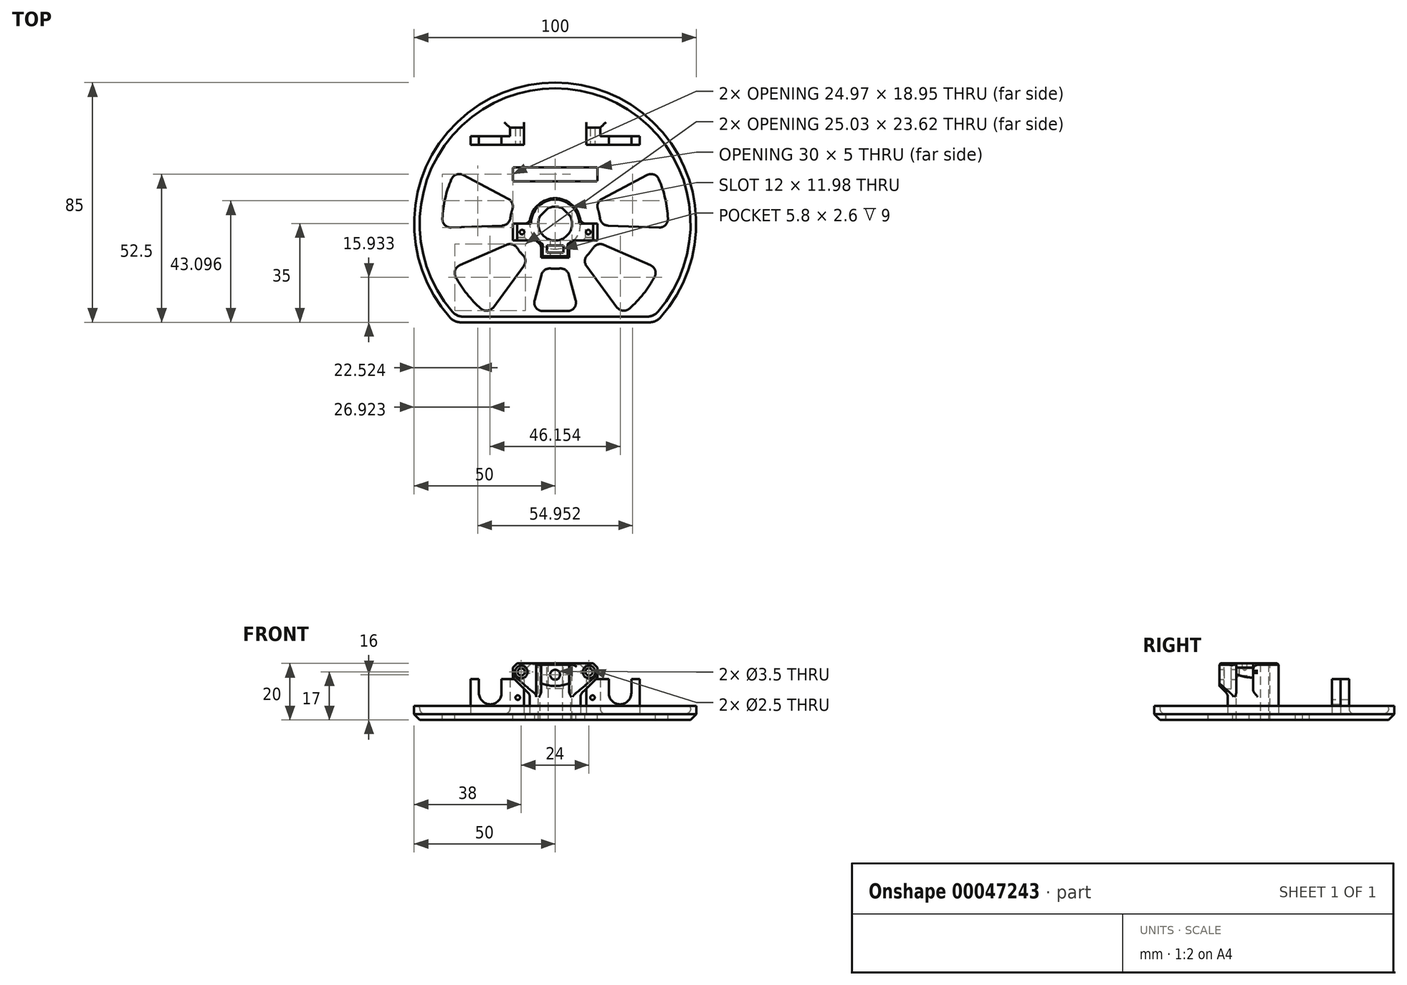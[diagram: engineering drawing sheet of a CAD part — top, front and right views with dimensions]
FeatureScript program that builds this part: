
annotation { "Feature Type Name" : "Feature", "Feature Type Description" : "" }
export const myFeature = defineFeature(function(context is Context, id is Id, definition is map)
    precondition{}
    {
        {
            var Q0;
            Q0=qCreatedBy(makeId("Top.planeOp"),FACE);
            var sketch = newSketch(context, id + "F0", { "sketchPlane" : qUnion([Q0])});
            skArc(sketch, "E0", {"start": v(35.7, -35) * mm, "mid": v(0, 50) * mm, "end": v(-35.7, -35) * mm});
            skLineSegment(sketch, "E1", {"start": v(0, 0) * mm, "end": v(0, -35) * mm, "construction": true});
            skLineSegment(sketch, "E2", {"start": v(0, -35) * mm, "end": v(35.7, -35) * mm});
            skLineSegment(sketch, "E3", {"start": v(0, -35) * mm, "end": v(-35.7, -35) * mm});
            skSolve(sketch);
        }
        {
            var Q0;
            Q0 = qSketchRegion(id + "F0", true);
            extrude(context, id + "F1", {"entities" : qUnion([Q0]), "depth" : 5 * mm});
        }
        {
            var Q0;
            Q0=makeQuery(id+"F1.opExtrude","CAP_FACE",FACE,{"disambiguationData":[OSD([sQuery(id+"F0.wireOp",EDGE,"E0")])],"isStart":false});
            var sketch = newSketch(context, id + "F2", { "sketchPlane" : qUnion([Q0])});
            skArc(sketch, "E4", {"start": v(32.85, -35) * mm, "mid": v(0, 48) * mm, "end": v(-32.85, -35) * mm});
            skLineSegment(sketch, "E5.0", {"start": v(32.85, -35) * mm, "end": v(-32.85, -35) * mm, "construction": true});
            skLineSegment(sketch, "E6.0", {"start": v(32.85, -33) * mm, "end": v(-32.85, -33) * mm});
            skLineSegment(sketch, "E7", {"start": v(-32.85, -33) * mm, "end": v(-34.86, -33) * mm});
            skLineSegment(sketch, "E8", {"start": v(32.85, -33) * mm, "end": v(34.86, -33) * mm});
            skSolve(sketch);
        }
        {
            var Q0;
            Q0 = qSketchRegion(id + "F2", true);
            extrude(context, id + "F3", {"entities" : qUnion([Q0]), "operationType" : NewBodyOperationType.REMOVE, "oppositeDirection" : true, "depth" : 3 * mm});
        }
        {
            var Q0;
            Q0=makeQuery(id+"F3.boolean.opBoolean","COPY",EDGE,{"derivedFrom":makeQuery(id+"F3.opExtrude","SWEPT_EDGE",EDGE,{"disambiguationData":[OSD([sQuery(id+"F2.wireOp",EDGE,"E4"),sQuery(id+"F2.wireOp",EDGE,"E7")])]})});
            var Q1;
            Q1=makeQuery(id+"F3.boolean.opBoolean","COPY",EDGE,{"derivedFrom":makeQuery(id+"F3.opExtrude","SWEPT_EDGE",EDGE,{"disambiguationData":[OSD([sQuery(id+"F2.wireOp",EDGE,"E4"),sQuery(id+"F2.wireOp",EDGE,"E8")])]})});
            var Q2;
            Q2=makeQuery(id+"F1.opExtrude","SWEPT_EDGE",EDGE,{"disambiguationData":[OSD([sQuery(id+"F0.wireOp",EDGE,"E0"),sQuery(id+"F0.wireOp",EDGE,"E3")])]});
            var Q3;
            Q3=makeQuery(id+"F1.opExtrude","SWEPT_EDGE",EDGE,{"disambiguationData":[OSD([sQuery(id+"F0.wireOp",EDGE,"E0"),sQuery(id+"F0.wireOp",EDGE,"E2")])]});
            fillet(context, id + "F4", {"entities" : qUnion([Q0, Q1, Q2, Q3]), "radius" : 5 * mm, "tangentPropagation" : true, "allowEdgeOverflow" : false});
        }
        {
            var Q0;
            Q0=makeQuery(id+"F3.boolean.opBoolean","COPY",EDGE,{"derivedFrom":makeQuery(id+"F3.opExtrude","CAP_EDGE",EDGE,{"disambiguationData":[OSD([sQuery(id+"F2.wireOp",EDGE,"E4")])],"isStart":false})});
            var Q1;
            Q1=makeQuery(id+"F3.boolean.opBoolean","COPY",EDGE,{"derivedFrom":makeQuery(id+"F3.opExtrude","CAP_EDGE",EDGE,{"disambiguationData":[OSD([sQuery(id+"F2.wireOp",EDGE,"E6.0"),sQuery(id+"F2.wireOp",EDGE,"E7"),sQuery(id+"F2.wireOp",EDGE,"E8")])],"isStart":false})});
            fillet(context, id + "F5", {"entities" : qUnion([Q0, Q1]), "radius" : 2 * mm, "tangentPropagation" : true, "allowEdgeOverflow" : false});
        }
        {
            var Q0;
            Q0=makeQuery(id+"F1.opExtrude","CAP_EDGE",EDGE,{"disambiguationData":[OSD([sQuery(id+"F0.wireOp",EDGE,"E0")])],"isStart":true});
            chamfer(context, id + "F6", {"entities" : qUnion([Q0]), "width" : 2 * mm, "tangentPropagation" : true});
        }
        {
            var Q0;
            Q0=makeQuery(id+"F3.boolean.opBoolean","COPY",FACE,{"derivedFrom":makeQuery(id+"F3.opExtrude","CAP_FACE",FACE,{"disambiguationData":[OSD([sQuery(id+"F2.wireOp",EDGE,"E4")])],"isStart":false})});
            var sketch = newSketch(context, id + "F7", { "sketchPlane" : qUnion([Q0])});
            skCircle(sketch, "E9", {"center": v(0, 0) * mm, "radius": 6 * mm});
            skCircle(sketch, "E10.0", {"center": v(0, 0) * mm, "radius": 50 * mm, "construction": true});
            skLineSegment(sketch, "E11", {"start": v(0, 0) * mm, "end": v(0, -50) * mm, "construction": true});
            skArc(sketch, "E12.0", {"start": v(-10.35, -38.64) * mm, "mid": v(0, -40) * mm, "end": v(10.35, -38.64) * mm, "construction": true});
            skArc(sketch, "E13.0", {"start": v(-4.14, -15.45) * mm, "mid": v(0, -16) * mm, "end": v(4.14, -15.45) * mm});
            skLineSegment(sketch, "E14.trimOffspring", {"start": v(4.14, -15.45) * mm, "end": v(10.35, -38.64) * mm});
            skLineSegment(sketch, "E15.trimOffspring", {"start": v(-4.14, -15.45) * mm, "end": v(-10.35, -38.64) * mm});
            skLineSegment(sketch, "E16.1.0", {"start": v(9.5, -12.87) * mm, "end": v(23.75, -32.18) * mm});
            skLineSegment(sketch, "E16.1.1", {"start": v(14.66, -6.4) * mm, "end": v(36.66, -16) * mm});
            skArc(sketch, "E16.1.2", {"start": v(9.5, -12.87) * mm, "mid": v(12.5, -9.98) * mm, "end": v(14.66, -6.4) * mm});
            skArc(sketch, "E16.1.3", {"start": v(23.75, -32.18) * mm, "mid": v(31.27, -24.94) * mm, "end": v(36.66, -16) * mm});
            skLineSegment(sketch, "E16.2.0", {"start": v(15.99, -0.6) * mm, "end": v(39.97, -1.5) * mm});
            skLineSegment(sketch, "E16.2.1", {"start": v(14.15, 7.48) * mm, "end": v(35.36, 18.7) * mm});
            skArc(sketch, "E16.2.2", {"start": v(15.99, -0.6) * mm, "mid": v(15.6, 3.56) * mm, "end": v(14.15, 7.48) * mm});
            skArc(sketch, "E16.2.3", {"start": v(39.97, -1.5) * mm, "mid": v(39, 8.9) * mm, "end": v(35.36, 18.7) * mm});
            skLineSegment(sketch, "E16.5.0", {"start": v(-14.15, 7.48) * mm, "end": v(-35.36, 18.7) * mm});
            skLineSegment(sketch, "E16.5.1", {"start": v(-15.99, -0.6) * mm, "end": v(-39.97, -1.5) * mm});
            skArc(sketch, "E16.5.2", {"start": v(-14.15, 7.48) * mm, "mid": v(-15.6, 3.56) * mm, "end": v(-15.99, -0.6) * mm});
            skArc(sketch, "E16.5.3", {"start": v(-35.36, 18.7) * mm, "mid": v(-39, 8.9) * mm, "end": v(-39.97, -1.5) * mm});
            skLineSegment(sketch, "E16.6.0", {"start": v(-14.66, -6.4) * mm, "end": v(-36.66, -16) * mm});
            skLineSegment(sketch, "E16.6.1", {"start": v(-9.5, -12.87) * mm, "end": v(-23.75, -32.18) * mm});
            skArc(sketch, "E16.6.2", {"start": v(-14.66, -6.4) * mm, "mid": v(-12.5, -9.98) * mm, "end": v(-9.5, -12.87) * mm});
            skArc(sketch, "E16.6.3", {"start": v(-36.66, -16) * mm, "mid": v(-31.27, -24.94) * mm, "end": v(-23.75, -32.18) * mm});
            skLineSegment(sketch, "E17.trimOffspring", {"start": v(-8.3, -31) * mm, "end": v(8.3, -31) * mm});
            skSolve(sketch);
        }
        {
            var Q0;
            Q0 = qSketchRegion(id + "F7", true);
            extrude(context, id + "F8", {"entities" : qUnion([Q0]), "operationType" : NewBodyOperationType.REMOVE, "oppositeDirection" : true, "depth" : 25 * mm});
        }
        {
            var Q0;
            Q0=makeQuery(id+"F8.boolean.opBoolean","COPY",EDGE,{"derivedFrom":makeQuery(id+"F8.opExtrude","SWEPT_EDGE",EDGE,{"disambiguationData":[OSD([sQuery(id+"F7.wireOp",EDGE,"E16.6.1"),sQuery(id+"F7.wireOp",EDGE,"E16.6.2")])]})});
            var Q1;
            Q1=makeQuery(id+"F8.boolean.opBoolean","COPY",EDGE,{"derivedFrom":makeQuery(id+"F8.opExtrude","SWEPT_EDGE",EDGE,{"disambiguationData":[OSD([sQuery(id+"F7.wireOp",EDGE,"E16.6.0"),sQuery(id+"F7.wireOp",EDGE,"E16.6.2")])]})});
            var Q2;
            Q2=makeQuery(id+"F8.boolean.opBoolean","COPY",EDGE,{"derivedFrom":makeQuery(id+"F8.opExtrude","SWEPT_EDGE",EDGE,{"disambiguationData":[OSD([sQuery(id+"F7.wireOp",EDGE,"E16.6.0"),sQuery(id+"F7.wireOp",EDGE,"E16.6.3")])]})});
            var Q3;
            Q3=makeQuery(id+"F8.boolean.opBoolean","COPY",EDGE,{"derivedFrom":makeQuery(id+"F8.opExtrude","SWEPT_EDGE",EDGE,{"disambiguationData":[OSD([sQuery(id+"F7.wireOp",EDGE,"E16.6.1"),sQuery(id+"F7.wireOp",EDGE,"E16.6.3")])]})});
            var Q4;
            Q4=makeQuery(id+"F8.boolean.opBoolean","COPY",EDGE,{"derivedFrom":makeQuery(id+"F8.opExtrude","SWEPT_EDGE",EDGE,{"disambiguationData":[OSD([sQuery(id+"F7.wireOp",EDGE,"E12.0"),sQuery(id+"F7.wireOp",EDGE,"E15.trimOffspring")])]})});
            var Q5;
            Q5=makeQuery(id+"F8.boolean.opBoolean","COPY",EDGE,{"derivedFrom":makeQuery(id+"F8.opExtrude","SWEPT_EDGE",EDGE,{"disambiguationData":[OSD([sQuery(id+"F7.wireOp",EDGE,"E16.1.0"),sQuery(id+"F7.wireOp",EDGE,"E16.1.2")])]})});
            var Q6;
            Q6=makeQuery(id+"F8.boolean.opBoolean","COPY",EDGE,{"derivedFrom":makeQuery(id+"F8.opExtrude","SWEPT_EDGE",EDGE,{"disambiguationData":[OSD([sQuery(id+"F7.wireOp",EDGE,"E16.2.0"),sQuery(id+"F7.wireOp",EDGE,"E16.2.2")])]})});
            var Q7;
            Q7=makeQuery(id+"F8.boolean.opBoolean","COPY",EDGE,{"derivedFrom":makeQuery(id+"F8.opExtrude","SWEPT_EDGE",EDGE,{"disambiguationData":[OSD([sQuery(id+"F7.wireOp",EDGE,"E13.0"),sQuery(id+"F7.wireOp",EDGE,"E14.trimOffspring")])]})});
            var Q8;
            Q8=makeQuery(id+"F8.boolean.opBoolean","COPY",EDGE,{"derivedFrom":makeQuery(id+"F8.opExtrude","SWEPT_EDGE",EDGE,{"disambiguationData":[OSD([sQuery(id+"F7.wireOp",EDGE,"E16.2.1"),sQuery(id+"F7.wireOp",EDGE,"E16.2.3")])]})});
            var Q9;
            Q9=makeQuery(id+"F8.boolean.opBoolean","COPY",EDGE,{"derivedFrom":makeQuery(id+"F8.opExtrude","SWEPT_EDGE",EDGE,{"disambiguationData":[OSD([sQuery(id+"F7.wireOp",EDGE,"E16.1.1"),sQuery(id+"F7.wireOp",EDGE,"E16.1.3")])]})});
            var Q10;
            Q10=makeQuery(id+"F8.boolean.opBoolean","COPY",EDGE,{"derivedFrom":makeQuery(id+"F8.opExtrude","SWEPT_EDGE",EDGE,{"disambiguationData":[OSD([sQuery(id+"F7.wireOp",EDGE,"E12.0"),sQuery(id+"F7.wireOp",EDGE,"E14.trimOffspring")])]})});
            var Q11;
            Q11=makeQuery(id+"F8.boolean.opBoolean","COPY",EDGE,{"derivedFrom":makeQuery(id+"F8.opExtrude","SWEPT_EDGE",EDGE,{"disambiguationData":[OSD([sQuery(id+"F7.wireOp",EDGE,"E16.1.0"),sQuery(id+"F7.wireOp",EDGE,"E16.1.3")])]})});
            var Q12;
            Q12=makeQuery(id+"F8.boolean.opBoolean","COPY",EDGE,{"derivedFrom":makeQuery(id+"F8.opExtrude","SWEPT_EDGE",EDGE,{"disambiguationData":[OSD([sQuery(id+"F7.wireOp",EDGE,"E16.3.0"),sQuery(id+"F7.wireOp",EDGE,"E16.3.2")])]})});
            var Q13;
            Q13=makeQuery(id+"F8.boolean.opBoolean","COPY",EDGE,{"derivedFrom":makeQuery(id+"F8.opExtrude","SWEPT_EDGE",EDGE,{"disambiguationData":[OSD([sQuery(id+"F7.wireOp",EDGE,"E16.4.1"),sQuery(id+"F7.wireOp",EDGE,"E16.4.2")])]})});
            var Q14;
            Q14=makeQuery(id+"F8.boolean.opBoolean","COPY",EDGE,{"derivedFrom":makeQuery(id+"F8.opExtrude","SWEPT_EDGE",EDGE,{"disambiguationData":[OSD([sQuery(id+"F7.wireOp",EDGE,"E16.5.1"),sQuery(id+"F7.wireOp",EDGE,"E16.5.2")])]})});
            var Q15;
            Q15=makeQuery(id+"F8.boolean.opBoolean","COPY",EDGE,{"derivedFrom":makeQuery(id+"F8.opExtrude","SWEPT_EDGE",EDGE,{"disambiguationData":[OSD([sQuery(id+"F7.wireOp",EDGE,"E16.5.0"),sQuery(id+"F7.wireOp",EDGE,"E16.5.2")])]})});
            var Q16;
            Q16=makeQuery(id+"F8.boolean.opBoolean","COPY",EDGE,{"derivedFrom":makeQuery(id+"F8.opExtrude","SWEPT_EDGE",EDGE,{"disambiguationData":[OSD([sQuery(id+"F7.wireOp",EDGE,"E16.3.0"),sQuery(id+"F7.wireOp",EDGE,"E16.3.3")])]})});
            var Q17;
            Q17=makeQuery(id+"F8.boolean.opBoolean","COPY",EDGE,{"derivedFrom":makeQuery(id+"F8.opExtrude","SWEPT_EDGE",EDGE,{"disambiguationData":[OSD([sQuery(id+"F7.wireOp",EDGE,"E16.4.0"),sQuery(id+"F7.wireOp",EDGE,"E16.4.3")])]})});
            var Q18;
            Q18=makeQuery(id+"F8.boolean.opBoolean","COPY",EDGE,{"derivedFrom":makeQuery(id+"F8.opExtrude","SWEPT_EDGE",EDGE,{"disambiguationData":[OSD([sQuery(id+"F7.wireOp",EDGE,"E16.4.0"),sQuery(id+"F7.wireOp",EDGE,"E16.4.2")])]})});
            var Q19;
            Q19=makeQuery(id+"F8.boolean.opBoolean","COPY",EDGE,{"derivedFrom":makeQuery(id+"F8.opExtrude","SWEPT_EDGE",EDGE,{"disambiguationData":[OSD([sQuery(id+"F7.wireOp",EDGE,"E16.3.1"),sQuery(id+"F7.wireOp",EDGE,"E16.3.2")])]})});
            var Q20;
            Q20=makeQuery(id+"F8.boolean.opBoolean","COPY",EDGE,{"derivedFrom":makeQuery(id+"F8.opExtrude","SWEPT_EDGE",EDGE,{"disambiguationData":[OSD([sQuery(id+"F7.wireOp",EDGE,"E16.5.1"),sQuery(id+"F7.wireOp",EDGE,"E16.5.3")])]})});
            var Q21;
            Q21=makeQuery(id+"F8.boolean.opBoolean","COPY",EDGE,{"derivedFrom":makeQuery(id+"F8.opExtrude","SWEPT_EDGE",EDGE,{"disambiguationData":[OSD([sQuery(id+"F7.wireOp",EDGE,"E16.5.0"),sQuery(id+"F7.wireOp",EDGE,"E16.5.3")])]})});
            var Q22;
            Q22=makeQuery(id+"F8.boolean.opBoolean","COPY",EDGE,{"derivedFrom":makeQuery(id+"F8.opExtrude","SWEPT_EDGE",EDGE,{"disambiguationData":[OSD([sQuery(id+"F7.wireOp",EDGE,"E13.0"),sQuery(id+"F7.wireOp",EDGE,"E15.trimOffspring")])]})});
            var Q23;
            Q23=makeQuery(id+"F8.boolean.opBoolean","COPY",EDGE,{"derivedFrom":makeQuery(id+"F8.opExtrude","SWEPT_EDGE",EDGE,{"disambiguationData":[OSD([sQuery(id+"F7.wireOp",EDGE,"E16.3.1"),sQuery(id+"F7.wireOp",EDGE,"E16.3.3")])]})});
            var Q24;
            Q24=makeQuery(id+"F8.boolean.opBoolean","COPY",EDGE,{"derivedFrom":makeQuery(id+"F8.opExtrude","SWEPT_EDGE",EDGE,{"disambiguationData":[OSD([sQuery(id+"F7.wireOp",EDGE,"E16.2.1"),sQuery(id+"F7.wireOp",EDGE,"E16.2.2")])]})});
            var Q25;
            Q25=makeQuery(id+"F8.boolean.opBoolean","COPY",EDGE,{"derivedFrom":makeQuery(id+"F8.opExtrude","SWEPT_EDGE",EDGE,{"disambiguationData":[OSD([sQuery(id+"F7.wireOp",EDGE,"E16.1.1"),sQuery(id+"F7.wireOp",EDGE,"E16.1.2")])]})});
            var Q26;
            Q26=makeQuery(id+"F8.boolean.opBoolean","COPY",EDGE,{"derivedFrom":makeQuery(id+"F8.opExtrude","SWEPT_EDGE",EDGE,{"disambiguationData":[OSD([sQuery(id+"F7.wireOp",EDGE,"E16.2.0"),sQuery(id+"F7.wireOp",EDGE,"E16.2.3")])]})});
            var Q27;
            Q27=makeQuery(id+"F8.boolean.opBoolean","COPY",EDGE,{"derivedFrom":makeQuery(id+"F8.opExtrude","SWEPT_EDGE",EDGE,{"disambiguationData":[OSD([sQuery(id+"F7.wireOp",EDGE,"E16.4.1"),sQuery(id+"F7.wireOp",EDGE,"E16.4.3")])]})});
            var Q28;
            Q28=makeQuery(id+"F8.boolean.opBoolean","COPY",EDGE,{"derivedFrom":makeQuery(id+"F8.opExtrude","SWEPT_EDGE",EDGE,{"disambiguationData":[OSD([sQuery(id+"F2.wireOp",EDGE,"E4"),sQuery(id+"F2.wireOp",EDGE,"E6.0"),sQuery(id+"F2.wireOp",EDGE,"E7"),sQuery(id+"F2.wireOp",EDGE,"E8"),sQuery(id+"F7.wireOp",EDGE,"E15.trimOffspring"),sQuery(id+"F7.wireOp",EDGE,"E17.trimOffspring")])]})});
            var Q29;
            Q29=makeQuery(id+"F8.boolean.opBoolean","COPY",EDGE,{"derivedFrom":makeQuery(id+"F8.opExtrude","SWEPT_EDGE",EDGE,{"disambiguationData":[OSD([sQuery(id+"F2.wireOp",EDGE,"E4"),sQuery(id+"F2.wireOp",EDGE,"E6.0"),sQuery(id+"F2.wireOp",EDGE,"E7"),sQuery(id+"F2.wireOp",EDGE,"E8"),sQuery(id+"F7.wireOp",EDGE,"E14.trimOffspring"),sQuery(id+"F7.wireOp",EDGE,"E17.trimOffspring")])]})});
            fillet(context, id + "F9", {"entities" : qUnion([Q0, Q1, Q2, Q3, Q4, Q5, Q6, Q7, Q8, Q9, Q10, Q11, Q12, Q13, Q14, Q15, Q16, Q17, Q18, Q19, Q20, Q21, Q22, Q23, Q24, Q25, Q26, Q27, Q28, Q29]), "radius" : 3 * mm, "tangentPropagation" : true, "allowEdgeOverflow" : false});
        }
        {
            var Q0;
            Q0=qCreatedBy(makeId("Top.planeOp"),FACE);
            var sketch = newSketch(context, id + "F10", { "sketchPlane" : qUnion([Q0])});
            skLineSegment(sketch, "E18", {"start": v(2.59, 5.41) * mm, "end": v(5.41, 2.59) * mm});
            skLineSegment(sketch, "E19", {"start": v(-2.59, 5.41) * mm, "end": v(-5.41, 2.59) * mm});
            skLineSegment(sketch, "E20", {"start": v(0, -8) * mm, "end": v(0, 0) * mm});
            skCircle(sketch, "E21", {"center": v(0, 0) * mm, "radius": 9 * mm});
            skArc(sketch, "E22.0", {"start": v(2.59, 5.41) * mm, "mid": v(0, 6) * mm, "end": v(-2.59, 5.41) * mm});
            skArc(sketch, "E23.trimOffspring", {"start": v(-5.41, 2.59) * mm, "mid": v(0, -6) * mm, "end": v(5.41, 2.59) * mm});
            skLineSegment(sketch, "E24", {"start": v(0, 0) * mm, "end": v(-5, 0) * mm, "construction": true});
            skLineSegment(sketch, "E25", {"start": v(-5, 0) * mm, "end": v(-5, -12) * mm});
            skLineSegment(sketch, "E26", {"start": v(-5, -12) * mm, "end": v(5, -12) * mm});
            skLineSegment(sketch, "E27", {"start": v(5, -12) * mm, "end": v(5, 0) * mm});
            skLineSegment(sketch, "E28", {"start": v(5, 0) * mm, "end": v(0, 0) * mm, "construction": true});
            skLineSegment(sketch, "E29", {"start": v(-9, 0) * mm, "end": v(-15, 0) * mm});
            skLineSegment(sketch, "E30", {"start": v(-15, 0) * mm, "end": v(-15, -6) * mm});
            skLineSegment(sketch, "E31", {"start": v(-15, -6) * mm, "end": v(-6.7, -6) * mm});
            skLineSegment(sketch, "E32.MirrorCS", {"start": v(9, 0) * mm, "end": v(15, 0) * mm});
            skLineSegment(sketch, "E33.MirrorCS", {"start": v(15, -6) * mm, "end": v(6.7, -6) * mm});
            skLineSegment(sketch, "E34.MirrorCS", {"start": v(15, 0) * mm, "end": v(15, -6) * mm});
            skSolve(sketch);
        }
        {
            var Q0;
            {var subQ11=sQuery(id+"F10.wireOp",EDGE,"E18");Q0=makeQuery(id+"F10.imprint","IMPRINT",FACE,{"disambiguationData":[TD([[makeQuery(id+"F10.imprint","IMPRINT",EDGE,{"derivedFrom":subQ11}),1.0]])]});}
            var Q1;
            {var subQ3=sQuery(id+"F10.wireOp",EDGE,"E23.trimOffspring");var subQ5=makeQuery(id+"F10.imprint","IMPRINT",VERTEX,{"derivedFrom":subQ3});Q1=makeQuery(id+"F10.imprint","IMPRINT",FACE,{"disambiguationData":[TD([[makeQuery(id+"F10.imprint","IMPRINT",EDGE,{"disambiguationData":[TD([[subQ5,1.0]])],"derivedFrom":subQ3}),-1.0]])]});}
            var Q2;
            {var subQ5=sQuery(id+"F10.wireOp",EDGE,"E26");Q2=makeQuery(id+"F10.imprint","IMPRINT",FACE,{"disambiguationData":[TD([[makeQuery(id+"F10.imprint","IMPRINT",EDGE,{"derivedFrom":subQ5}),1.0]])]});}
            extrude(context, id + "F11", {"entities" : qUnion([Q0, Q1, Q2]), "operationType" : NewBodyOperationType.ADD, "depth" : 20 * mm});
        }
        {
            var Q0;
            Q0=makeQuery(id+"F11.opExtrude","CAP_FACE",FACE,{"disambiguationData":[OSD([sQuery(id+"F10.wireOp",EDGE,"E18"),sQuery(id+"F10.wireOp",EDGE,"E19"),sQuery(id+"F10.wireOp",EDGE,"E21"),sQuery(id+"F10.wireOp",EDGE,"E22.0"),sQuery(id+"F10.wireOp",EDGE,"E23.trimOffspring"),sQuery(id+"F10.wireOp",EDGE,"E25"),sQuery(id+"F10.wireOp",EDGE,"E26"),sQuery(id+"F10.wireOp",EDGE,"E27")])],"isStart":false});
            var sketch = newSketch(context, id + "F12", { "sketchPlane" : qUnion([Q0])});
            skLineSegment(sketch, "E35", {"start": v(0, -9) * mm, "end": v(2.9, -9) * mm, "construction": true});
            skLineSegment(sketch, "E36", {"start": v(0, -9) * mm, "end": v(-2.9, -9) * mm, "construction": true});
            skLineSegment(sketch, "E37", {"start": v(-2.9, -9) * mm, "end": v(-2.9, -7.7) * mm});
            skLineSegment(sketch, "E38", {"start": v(-2.9, -7.7) * mm, "end": v(2.9, -7.7) * mm});
            skLineSegment(sketch, "E39", {"start": v(2.9, -7.7) * mm, "end": v(2.9, -10.3) * mm});
            skLineSegment(sketch, "E40", {"start": v(2.9, -10.3) * mm, "end": v(-2.9, -10.3) * mm});
            skLineSegment(sketch, "E41", {"start": v(-2.9, -10.3) * mm, "end": v(-2.9, -9) * mm});
            skLineSegment(sketch, "E42", {"start": v(0, -12) * mm, "end": v(0, -9) * mm, "construction": true});
            skSolve(sketch);
        }
        {
            var Q0;
            Q0 = qSketchRegion(id + "F12", true);
            extrude(context, id + "F13", {"entities" : qUnion([Q0]), "operationType" : NewBodyOperationType.REMOVE, "oppositeDirection" : true, "depth" : 9 * mm});
        }
        {
            var Q0;
            Q0=makeQuery(id+"F11.opExtrude","SWEPT_FACE",FACE,{"disambiguationData":[OSD([sQuery(id+"F10.wireOp",EDGE,"E26")])]});
            var sketch = newSketch(context, id + "F14", { "sketchPlane" : qUnion([Q0])});
            skLineSegment(sketch, "E43", {"start": v(0, 20) * mm, "end": v(0, 16) * mm, "construction": true});
            skPoint(sketch, "E43.endSnap0", {"position": v(0, 20) * mm});
            skCircle(sketch, "E44", {"center": v(0, 16) * mm, "radius": 1.75 * mm});
            skSolve(sketch);
        }
        {
            var Q0;
            Q0 = qSketchRegion(id + "F14", true);
            extrude(context, id + "F15", {"entities" : qUnion([Q0]), "operationType" : NewBodyOperationType.REMOVE, "oppositeDirection" : true, "depth" : 10 * mm});
        }
        {
            var Q0;
            Q0=makeQuery(id+"F3.boolean.opBoolean","COPY",FACE,{"derivedFrom":makeQuery(id+"F3.opExtrude","CAP_FACE",FACE,{"disambiguationData":[OSD([sQuery(id+"F2.wireOp",EDGE,"E4")])],"isStart":false})});
            var sketch = newSketch(context, id + "F16", { "sketchPlane" : qUnion([Q0])});
            skCircle(sketch, "E45.0", {"center": v(0, 0) * mm, "radius": 48 * mm, "construction": true});
            skArc(sketch, "E45.1", {"start": v(5, -7.48) * mm, "mid": v(0, 9) * mm, "end": v(-5, -7.48) * mm, "construction": true});
            skLineSegment(sketch, "E46", {"start": v(0, -9) * mm, "end": v(0, -46) * mm, "construction": true});
            skLineSegment(sketch, "E47", {"start": v(0, -27.5) * mm, "end": v(9, -27.5) * mm, "construction": true});
            skPoint(sketch, "E47.endSnap0", {"position": v(0, -27.5) * mm});
            skLineSegment(sketch, "E48", {"start": v(0, -27.5) * mm, "end": v(-9, -27.5) * mm, "construction": true});
            skLineSegment(sketch, "E49", {"start": v(-9, -27.5) * mm, "end": v(-9, -20.5) * mm});
            skLineSegment(sketch, "E50", {"start": v(-9, -27.5) * mm, "end": v(-9, -34.5) * mm});
            skLineSegment(sketch, "E51", {"start": v(9, -20.5) * mm, "end": v(9, -34.5) * mm});
            skLineSegment(sketch, "E52", {"start": v(9, -34.5) * mm, "end": v(13, -34.5) * mm});
            skLineSegment(sketch, "E53", {"start": v(13, -34.5) * mm, "end": v(13, -20.5) * mm});
            skLineSegment(sketch, "E54", {"start": v(13, -20.5) * mm, "end": v(9, -20.5) * mm});
            skLineSegment(sketch, "E55", {"start": v(-9, -20.5) * mm, "end": v(-13, -20.5) * mm});
            skLineSegment(sketch, "E56", {"start": v(-13, -20.5) * mm, "end": v(-13, -34.5) * mm});
            skLineSegment(sketch, "E57", {"start": v(-13, -34.5) * mm, "end": v(-9, -34.5) * mm});
            skSolve(sketch);
        }
        {
            var Q0;
            {var subQ0=sQuery(id+"F10.wireOp",EDGE,"E32.MirrorCS");Q0=makeQuery(id+"F10.imprint","IMPRINT",FACE,{"disambiguationData":[TD([[makeQuery(id+"F10.imprint","IMPRINT",EDGE,{"derivedFrom":subQ0}),-1.0]])]});}
            var Q1;
            {var subQ0=sQuery(id+"F10.wireOp",EDGE,"E29");Q1=makeQuery(id+"F10.imprint","IMPRINT",FACE,{"disambiguationData":[TD([[makeQuery(id+"F10.imprint","IMPRINT",EDGE,{"derivedFrom":subQ0}),1.0]])]});}
            extrude(context, id + "F17", {"entities" : qUnion([Q0, Q1]), "operationType" : NewBodyOperationType.ADD, "depth" : 20 * mm});
        }
        {
            var Q0;
            Q0=makeQuery(id+"F17.opExtrude","SWEPT_FACE",FACE,{"disambiguationData":[OSD([sQuery(id+"F10.wireOp",EDGE,"E29")])]});
            var sketch = newSketch(context, id + "F18", { "sketchPlane" : qUnion([Q0])});
            skLineSegment(sketch, "E58.0", {"start": v(-50, 5) * mm, "end": v(50, 5) * mm, "construction": true});
            skLineSegment(sketch, "E58.1", {"start": v(-9, 20) * mm, "end": v(-15, 20) * mm, "construction": true});
            skLineSegment(sketch, "E58.2", {"start": v(9, 20) * mm, "end": v(15, 20) * mm, "construction": true});
            skCircle(sketch, "E59", {"center": v(-12, 17) * mm, "radius": 1.25 * mm});
            skCircle(sketch, "E60", {"center": v(12, 17) * mm, "radius": 1.25 * mm});
            skLineSegment(sketch, "E61", {"start": v(-12, 20) * mm, "end": v(-12, 17) * mm, "construction": true});
            skLineSegment(sketch, "E62", {"start": v(12, 20) * mm, "end": v(12, 17) * mm, "construction": true});
            skSolve(sketch);
        }
        {
            var Q0;
            Q0 = qSketchRegion(id + "F18", true);
            extrude(context, id + "F19", {"entities" : qUnion([Q0]), "operationType" : NewBodyOperationType.REMOVE, "oppositeDirection" : true, "depth" : 10 * mm});
        }
        {
            var Q0;
            Q0=makeQuery(id+"F17.opExtrude","CAP_FACE",FACE,{"disambiguationData":[OSD([sQuery(id+"F10.wireOp",EDGE,"E21"),sQuery(id+"F10.wireOp",EDGE,"E32.MirrorCS"),sQuery(id+"F10.wireOp",EDGE,"E33.MirrorCS"),sQuery(id+"F10.wireOp",EDGE,"E34.MirrorCS")])],"isStart":false});
            var sketch = newSketch(context, id + "F20", { "sketchPlane" : qUnion([Q0])});
            skLineSegment(sketch, "E63", {"start": v(15, -3) * mm, "end": v(8.49, -3) * mm, "construction": true});
            skLineSegment(sketch, "E64", {"start": v(0, 0) * mm, "end": v(0, -4.37) * mm, "construction": true});
            skCircle(sketch, "E65", {"center": v(11.74, -3) * mm, "radius": 0.8 * mm});
            skCircle(sketch, "E66.MirrorC", {"center": v(-11.74, -3) * mm, "radius": 0.8 * mm});
            skSolve(sketch);
        }
        {
            var Q0;
            Q0 = qSketchRegion(id + "F20", true);
            extrude(context, id + "F21", {"entities" : qUnion([Q0]), "operationType" : NewBodyOperationType.REMOVE, "oppositeDirection" : true, "depth" : 3 * mm});
        }
        {
            var Q0;
            Q0=makeQuery(id+"F17.opExtrude","CAP_EDGE",EDGE,{"disambiguationData":[OSD([sQuery(id+"F10.wireOp",EDGE,"E30")])],"isStart":false});
            var Q1;
            Q1=makeQuery(id+"F17.opExtrude","CAP_EDGE",EDGE,{"disambiguationData":[OSD([sQuery(id+"F10.wireOp",EDGE,"E34.MirrorCS")])],"isStart":false});
            chamfer(context, id + "F22", {"entities" : qUnion([Q0, Q1]), "width" : 1.5 * mm, "tangentPropagation" : true});
        }
        {
            var Q0;
            Q0=qCreatedBy(makeId("Top.planeOp"),FACE);
            var sketch = newSketch(context, id + "F23", { "sketchPlane" : qUnion([Q0])});
            skCircle(sketch, "E67.0", {"center": v(0, 0) * mm, "radius": 48 * mm, "construction": true});
            skLineSegment(sketch, "E68", {"start": v(0, 48) * mm, "end": v(0, 34) * mm, "construction": true});
            skLineSegment(sketch, "E69", {"start": v(0, 34) * mm, "end": v(11, 34) * mm});
            skLineSegment(sketch, "E70", {"start": v(11, 34) * mm, "end": v(11, 28) * mm});
            skLineSegment(sketch, "E71", {"start": v(11, 28) * mm, "end": v(16, 28) * mm});
            skLineSegment(sketch, "E72", {"start": v(16, 28) * mm, "end": v(16, 34) * mm});
            skLineSegment(sketch, "E73", {"start": v(16, 34) * mm, "end": v(11, 34) * mm});
            skLineSegment(sketch, "E74.MirrorCS", {"start": v(-11, 28) * mm, "end": v(-16, 28) * mm});
            skLineSegment(sketch, "E75.MirrorCS", {"start": v(-11, 34) * mm, "end": v(-11, 28) * mm});
            skLineSegment(sketch, "E76.MirrorCS", {"start": v(-16, 34) * mm, "end": v(-11, 34) * mm});
            skLineSegment(sketch, "E77.MirrorCS", {"start": v(-16, 28) * mm, "end": v(-16, 34) * mm});
            skLineSegment(sketch, "E78", {"start": v(-11, 28) * mm, "end": v(11, 28) * mm, "construction": true});
            skLineSegment(sketch, "E79", {"start": v(0, 28) * mm, "end": v(0, 16) * mm, "construction": true});
            skPoint(sketch, "E79.endSnap0", {"position": v(0, 28) * mm});
            skSolve(sketch);
        }
        {
            var Q0;
            Q0 = qSketchRegion(id + "F23", true);
            extrude(context, id + "F24", {"entities" : qUnion([Q0]), "operationType" : NewBodyOperationType.ADD, "depth" : 14.5 * mm});
        }
        {
            var Q0;
            Q0=makeQuery(id+"F0nIdXVJw5lt9VU_1.opFillet","SPLIT",FACE,{"disambiguationData":[OD(0.0)],"derivedFrom":makeQuery(id+"F3.boolean.opBoolean","COPY",FACE,{"derivedFrom":makeQuery(id+"F3.opExtrude","CAP_FACE",FACE,{"disambiguationData":[OSD([sQuery(id+"F2.wireOp",EDGE,"E4")])],"isStart":false})})});
            var sketch = newSketch(context, id + "F25", { "sketchPlane" : qUnion([Q0])});
            skLineSegment(sketch, "E80.0", {"start": v(-11, 28) * mm, "end": v(-16, 28) * mm, "construction": true});
            skLineSegment(sketch, "E80.1", {"start": v(11, 28) * mm, "end": v(16, 28) * mm, "construction": true});
            skLineSegment(sketch, "E81", {"start": v(-11, 28) * mm, "end": v(11, 28) * mm, "construction": true});
            skLineSegment(sketch, "E82", {"start": v(0, 28) * mm, "end": v(0, 15) * mm, "construction": true});
            skPoint(sketch, "E82.endSnap0", {"position": v(0, 28) * mm});
            skLineSegment(sketch, "E83", {"start": v(0, 15) * mm, "end": v(15, 15) * mm});
            skLineSegment(sketch, "E84", {"start": v(15, 15) * mm, "end": v(15, 20) * mm});
            skLineSegment(sketch, "E85", {"start": v(15, 20) * mm, "end": v(-15, 20) * mm});
            skLineSegment(sketch, "E86", {"start": v(-15, 20) * mm, "end": v(-15, 15) * mm});
            skLineSegment(sketch, "E87", {"start": v(-15, 15) * mm, "end": v(0, 15) * mm});
            skSolve(sketch);
        }
        {
            var Q0;
            Q0 = qSketchRegion(id + "F25", true);
            extrude(context, id + "F26", {"entities" : qUnion([Q0]), "operationType" : NewBodyOperationType.REMOVE, "oppositeDirection" : true, "depth" : 25 * mm});
        }
        {
            var Q0;
            Q0=makeQuery(id+"F26.boolean.opBoolean","COPY",EDGE,{"derivedFrom":makeQuery(id+"F26.opExtrude","SWEPT_EDGE",EDGE,{"disambiguationData":[OSD([sQuery(id+"F25.wireOp",EDGE,"E86"),sQuery(id+"F25.wireOp",EDGE,"E87")])]})});
            var Q1;
            Q1=makeQuery(id+"F26.boolean.opBoolean","COPY",EDGE,{"derivedFrom":makeQuery(id+"F26.opExtrude","SWEPT_EDGE",EDGE,{"disambiguationData":[OSD([sQuery(id+"F25.wireOp",EDGE,"E85"),sQuery(id+"F25.wireOp",EDGE,"E86")])]})});
            var Q2;
            Q2=makeQuery(id+"F26.boolean.opBoolean","COPY",EDGE,{"derivedFrom":makeQuery(id+"F26.opExtrude","SWEPT_EDGE",EDGE,{"disambiguationData":[OSD([sQuery(id+"F25.wireOp",EDGE,"E84"),sQuery(id+"F25.wireOp",EDGE,"E85")])]})});
            var Q3;
            Q3=makeQuery(id+"F26.boolean.opBoolean","COPY",EDGE,{"derivedFrom":makeQuery(id+"F26.opExtrude","SWEPT_EDGE",EDGE,{"disambiguationData":[OSD([sQuery(id+"F25.wireOp",EDGE,"E83"),sQuery(id+"F25.wireOp",EDGE,"E84")])]})});
            fillet(context, id + "F27", {"entities" : qUnion([Q0, Q1, Q2, Q3]), "radius" : .5 * mm, "tangentPropagation" : true, "allowEdgeOverflow" : false});
        }
        {
            var Q0;
            Q0=makeQuery(id+"F11.opExtrude","CAP_EDGE",EDGE,{"disambiguationData":[OSD([sQuery(id+"F10.wireOp",EDGE,"E21")])],"isStart":false});
            var Q1;
            {var subQ0=sQuery(id+"F10.wireOp",EDGE,"E27");var subQ1=sQuery(id+"F10.wireOp",EDGE,"E21");Q1=makeQuery(id+"F34.opFillet","BLEND_EDGE",EDGE,{"blendedFrom":[makeQuery(id+"F11.opExtrude","SWEPT_EDGE",EDGE,{"disambiguationData":[OSD([subQ1,subQ0])]}),makeQuery(id+"F11.opExtrude","CAP_FACE",FACE,{"disambiguationData":[OSD([sQuery(id+"F10.wireOp",EDGE,"E18"),sQuery(id+"F10.wireOp",EDGE,"E19"),subQ1,sQuery(id+"F10.wireOp",EDGE,"E22.0"),sQuery(id+"F10.wireOp",EDGE,"E23.trimOffspring"),sQuery(id+"F10.wireOp",EDGE,"E25"),sQuery(id+"F10.wireOp",EDGE,"E26"),subQ0])],"isStart":false})],"blendedInto":[makeQuery(id+"F11.opExtrude","CAP_FACE",FACE,{"disambiguationData":[OSD([sQuery(id+"F10.wireOp",EDGE,"E18"),sQuery(id+"F10.wireOp",EDGE,"E19"),subQ1,sQuery(id+"F10.wireOp",EDGE,"E22.0"),sQuery(id+"F10.wireOp",EDGE,"E23.trimOffspring"),sQuery(id+"F10.wireOp",EDGE,"E25"),sQuery(id+"F10.wireOp",EDGE,"E26"),subQ0])],"isStart":false})]});}
            var Q2;
            Q2=makeQuery(id+"F11.opExtrude","CAP_EDGE",EDGE,{"disambiguationData":[OSD([sQuery(id+"F10.wireOp",EDGE,"E27")])],"isStart":false});
            var Q3;
            Q3=makeQuery(id+"F11.opExtrude","CAP_EDGE",EDGE,{"disambiguationData":[OSD([sQuery(id+"F10.wireOp",EDGE,"E26")])],"isStart":false});
            var Q4;
            Q4=makeQuery(id+"F11.opExtrude","CAP_EDGE",EDGE,{"disambiguationData":[OSD([sQuery(id+"F10.wireOp",EDGE,"E25")])],"isStart":false});
            var Q5;
            {var subQ0=sQuery(id+"F10.wireOp",EDGE,"E25");var subQ1=sQuery(id+"F10.wireOp",EDGE,"E21");Q5=makeQuery(id+"F34.opFillet","BLEND_EDGE",EDGE,{"blendedFrom":[makeQuery(id+"F11.opExtrude","SWEPT_EDGE",EDGE,{"disambiguationData":[OSD([subQ1,subQ0])]}),makeQuery(id+"F11.opExtrude","CAP_FACE",FACE,{"disambiguationData":[OSD([sQuery(id+"F10.wireOp",EDGE,"E18"),sQuery(id+"F10.wireOp",EDGE,"E19"),subQ1,sQuery(id+"F10.wireOp",EDGE,"E22.0"),sQuery(id+"F10.wireOp",EDGE,"E23.trimOffspring"),subQ0,sQuery(id+"F10.wireOp",EDGE,"E26"),sQuery(id+"F10.wireOp",EDGE,"E27")])],"isStart":false})],"blendedInto":[makeQuery(id+"F11.opExtrude","CAP_FACE",FACE,{"disambiguationData":[OSD([sQuery(id+"F10.wireOp",EDGE,"E18"),sQuery(id+"F10.wireOp",EDGE,"E19"),subQ1,sQuery(id+"F10.wireOp",EDGE,"E22.0"),sQuery(id+"F10.wireOp",EDGE,"E23.trimOffspring"),subQ0,sQuery(id+"F10.wireOp",EDGE,"E26"),sQuery(id+"F10.wireOp",EDGE,"E27")])],"isStart":false})]});}
            chamfer(context, id + "F28", {"entities" : qUnion([Q0, Q1, Q2, Q3, Q4, Q5]), "width" : .5 * mm, "tangentPropagation" : true});
        }
        {
            var Q0;
            Q0=makeQuery(id+"F24.opExtrude","SWEPT_FACE",FACE,{"disambiguationData":[OSD([sQuery(id+"F23.wireOp",EDGE,"E74.MirrorCS")])]});
            var sketch = newSketch(context, id + "F29", { "sketchPlane" : qUnion([Q0])});
            skLineSegment(sketch, "E88", {"start": v(-13.25, 2) * mm, "end": v(-13.25, 7.9) * mm, "construction": true});
            skLineSegment(sketch, "E89", {"start": v(13.25, 2) * mm, "end": v(13.25, 7.9) * mm, "construction": true});
            skCircle(sketch, "E90", {"center": v(-13.25, 7.9) * mm, "radius": 0.8 * mm});
            skCircle(sketch, "E91", {"center": v(13.25, 7.9) * mm, "radius": 0.8 * mm});
            skLineSegment(sketch, "E92", {"start": v(-13.25, 2) * mm, "end": v(0, 2) * mm, "construction": true});
            skLineSegment(sketch, "E93", {"start": v(0, 2) * mm, "end": v(13.25, 2) * mm, "construction": true});
            skSolve(sketch);
        }
        {
            var Q0;
            Q0 = qSketchRegion(id + "F29", true);
            extrude(context, id + "F30", {"entities" : qUnion([Q0]), "operationType" : NewBodyOperationType.REMOVE, "oppositeDirection" : true, "depth" : 25 * mm});
        }
        {
            var Q0;
            Q0=makeQuery(id+"F17.opExtrude","SWEPT_FACE",FACE,{"disambiguationData":[OSD([sQuery(id+"F10.wireOp",EDGE,"E31")])]});
            var sketch = newSketch(context, id + "F31", { "sketchPlane" : qUnion([Q0])});
            skLineSegment(sketch, "E94", {"start": v(-12, 17) * mm, "end": v(-12, 12) * mm});
            skLineSegment(sketch, "E95", {"start": v(-12, 12) * mm, "end": v(-15, 15) * mm});
            skLineSegment(sketch, "E96", {"start": v(-12, 12) * mm, "end": v(-6.7, 6.7) * mm});
            skLineSegment(sketch, "E97", {"start": v(-6.7, 6.7) * mm, "end": v(-6.7, 2) * mm});
            skLineSegment(sketch, "E98", {"start": v(-6.7, 2) * mm, "end": v(-15, 2) * mm});
            skLineSegment(sketch, "E99", {"start": v(-15, 2) * mm, "end": v(-15, 15) * mm});
            skSolve(sketch);
        }
        {
            var Q0;
            Q0=qCreatedBy(makeId("Front.planeOp"),FACE);
            var sketch = newSketch(context, id + "F32", { "sketchPlane" : qUnion([Q0])});
            skLineSegment(sketch, "E100.0", {"start": v(-9, 2) * mm, "end": v(-15, 2) * mm});
            skLineSegment(sketch, "E100.2", {"start": v(-12, 12) * mm, "end": v(-9, 9) * mm});
            skLineSegment(sketch, "E100.3", {"start": v(-12, 12) * mm, "end": v(-15, 15) * mm});
            skLineSegment(sketch, "E101", {"start": v(0, 0) * mm, "end": v(0, 26.74) * mm, "construction": true});
            skLineSegment(sketch, "E102", {"start": v(-15, 15) * mm, "end": v(-17.62, 17.62) * mm});
            skLineSegment(sketch, "E103", {"start": v(-17.62, 17.62) * mm, "end": v(-17.62, 2) * mm});
            skLineSegment(sketch, "E104", {"start": v(-17.62, 2) * mm, "end": v(-15, 2) * mm});
            skLineSegment(sketch, "E105.0", {"start": v(-9, 9) * mm, "end": v(-9, 2) * mm});
            skPoint(sketch, "E100.4.end.orphan", {"position": v(-6.7, 2) * mm});
            skPoint(sketch, "E100.4.start.orphan", {"position": v(-6.7, 6.7) * mm});
            skPoint(sketch, "E106.orphan", {"position": v(-9, 19.5) * mm});
            skSolve(sketch);
        }
        {
            var Q0;
            Q0 = qSketchRegion(id + "F32", true);
            var Q1;
            Q1=sQuery(id+"F32.wireOp",EDGE,"E101");
            revolve(context, id + "F33", {"operationType" : NewBodyOperationType.REMOVE, "entities" : qUnion([Q0]), "axis" : qUnion([Q1]), "revolveType" : RevolveType.FULL, "oppositeDirection" : true});
        }
        {
            var Q0;
            Q0=makeQuery(id+"F11.opExtrude","SWEPT_EDGE",EDGE,{"disambiguationData":[OSD([sQuery(id+"F10.wireOp",EDGE,"E21"),sQuery(id+"F10.wireOp",EDGE,"E27")])]});
            var Q1;
            Q1=makeQuery(id+"F11.opExtrude","SWEPT_EDGE",EDGE,{"disambiguationData":[OSD([sQuery(id+"F10.wireOp",EDGE,"E21"),sQuery(id+"F10.wireOp",EDGE,"E25")])]});
            var Q2;
            Q2=makeQuery(id+"F17.opExtrude","SWEPT_EDGE",EDGE,{"disambiguationData":[OSD([sQuery(id+"F10.wireOp",EDGE,"E21"),sQuery(id+"F10.wireOp",EDGE,"E31")])]});
            var Q3;
            Q3=makeQuery(id+"F17.opExtrude","SWEPT_EDGE",EDGE,{"disambiguationData":[OSD([sQuery(id+"F10.wireOp",EDGE,"E21"),sQuery(id+"F10.wireOp",EDGE,"E33.MirrorCS")])]});
            var Q4;
            Q4=makeQuery(id+"F17.opExtrude","SWEPT_EDGE",EDGE,{"disambiguationData":[OSD([sQuery(id+"F10.wireOp",EDGE,"E21"),sQuery(id+"F10.wireOp",EDGE,"E29")])]});
            var Q5;
            Q5=makeQuery(id+"F17.opExtrude","SWEPT_EDGE",EDGE,{"disambiguationData":[OSD([sQuery(id+"F10.wireOp",EDGE,"E21"),sQuery(id+"F10.wireOp",EDGE,"E32.MirrorCS")])]});
            var Q6;
            Q6=makeQuery(id+"F33.boolean.opBoolean","COPY",EDGE,{"derivedFrom":makeQuery(id+"F33.opRevolve","SWEPT_EDGE",EDGE,{"disambiguationData":[OSD([sQuery(id+"F32.wireOp",EDGE,"E100.0"),sQuery(id+"F32.wireOp",EDGE,"E100.4")])]})});
            var Q7;
            Q7=makeQuery(id+"F33.boolean.opBoolean","COPY",EDGE,{"derivedFrom":makeQuery(id+"F33.opRevolve","SWEPT_EDGE",EDGE,{"disambiguationData":[OSD([sQuery(id+"F32.wireOp",EDGE,"E100.2"),sQuery(id+"F32.wireOp",EDGE,"E100.4")])]})});
            fillet(context, id + "F34", {"entities" : qUnion([Q0, Q1, Q2, Q3, Q4, Q5, Q6, Q7]), "radius" : 2 * mm, "tangentPropagation" : true, "allowEdgeOverflow" : false});
        }
        {
            var Q0;
            Q0=makeQuery(id+"F19.boolean.opBoolean","INTERSECT",EDGE,{"derivedFrom":[makeQuery(id+"F17.opExtrude","SWEPT_FACE",FACE,{"disambiguationData":[OSD([sQuery(id+"F10.wireOp",EDGE,"E31")])]}),makeQuery(id+"F19.opExtrude","SWEPT_FACE",FACE,{"disambiguationData":[OSD([sQuery(id+"F18.wireOp",EDGE,"E60")])]})]});
            var Q1;
            Q1=makeQuery(id+"F19.boolean.opBoolean","INTERSECT",EDGE,{"derivedFrom":[makeQuery(id+"F17.opExtrude","SWEPT_FACE",FACE,{"disambiguationData":[OSD([sQuery(id+"F10.wireOp",EDGE,"E33.MirrorCS")])]}),makeQuery(id+"F19.opExtrude","SWEPT_FACE",FACE,{"disambiguationData":[OSD([sQuery(id+"F18.wireOp",EDGE,"E59")])]})]});
            chamfer(context, id + "F35", {"entities" : qUnion([Q0, Q1]), "width" : 1 * mm, "tangentPropagation" : true});
        }
        {
            var Q0;
            {var subQ42=sQuery(id+"F16.wireOp",EDGE,"E49");Q0=makeQuery(id+"F16.imprint","IMPRINT",FACE,{"disambiguationData":[TD([[makeQuery(id+"F16.imprint","IMPRINT",EDGE,{"derivedFrom":subQ42}),-1.0]])]});}
            var sketch = newSketch(context, id + "F36", { "sketchPlane" : qUnion([Q0])});
            skLineSegment(sketch, "E107", {"start": v(-30, 31) * mm, "end": v(-16, 31) * mm});
            skLineSegment(sketch, "E108", {"start": v(30, 31) * mm, "end": v(16, 31) * mm});
            skLineSegment(sketch, "E109", {"start": v(-16, 31) * mm, "end": v(0, 31) * mm, "construction": true});
            skLineSegment(sketch, "E110", {"start": v(-30, 31) * mm, "end": v(-30, 28) * mm});
            skLineSegment(sketch, "E111", {"start": v(-30, 28) * mm, "end": v(-16, 28) * mm});
            skLineSegment(sketch, "E112", {"start": v(-16, 28) * mm, "end": v(-16, 31) * mm});
            skLineSegment(sketch, "E113", {"start": v(0, 31) * mm, "end": v(16, 31) * mm, "construction": true});
            skLineSegment(sketch, "E114", {"start": v(16, 31) * mm, "end": v(16, 28) * mm});
            skLineSegment(sketch, "E115", {"start": v(16, 28) * mm, "end": v(30, 28) * mm});
            skLineSegment(sketch, "E116", {"start": v(30, 28) * mm, "end": v(30, 31) * mm});
            skSolve(sketch);
        }
        {
            var Q0;
            Q0 = qSketchRegion(id + "F36", true);
            extrude(context, id + "F37", {"entities" : qUnion([Q0]), "operationType" : NewBodyOperationType.ADD, "depth" : 12.5 * mm});
        }
        {
            var Q0;
            Q0=makeQuery(id+"F37.opExtrude","SWEPT_FACE",FACE,{"disambiguationData":[OSD([sQuery(id+"F36.wireOp",EDGE,"E111")])]});
            var sketch = newSketch(context, id + "F38", { "sketchPlane" : qUnion([Q0])});
            skLineSegment(sketch, "E117", {"start": v(-27, 9.5) * mm, "end": v(-27, 14.5) * mm});
            skLineSegment(sketch, "E118", {"start": v(-27, 14.5) * mm, "end": v(-19, 14.5) * mm});
            skArc(sketch, "E119.MirrorCS", {"start": v(-19, 9.5) * mm, "mid": v(-23, 5.5) * mm, "end": v(-27, 9.5) * mm});
            skLineSegment(sketch, "E120.MirrorCS", {"start": v(-19, 9.5) * mm, "end": v(-19, 14.5) * mm});
            skArc(sketch, "E121.MirrorCS", {"start": v(27, 9.5) * mm, "mid": v(23, 5.5) * mm, "end": v(19, 9.5) * mm});
            skLineSegment(sketch, "E122.MirrorCS", {"start": v(27, 9.5) * mm, "end": v(27, 14.5) * mm});
            skLineSegment(sketch, "E123.MirrorCS", {"start": v(27, 14.5) * mm, "end": v(19, 14.5) * mm});
            skLineSegment(sketch, "E124.MirrorCS", {"start": v(19, 9.5) * mm, "end": v(19, 14.5) * mm});
            skLineSegment(sketch, "E125", {"start": v(-30, 14.5) * mm, "end": v(-27, 14.5) * mm});
            skLineSegment(sketch, "E126", {"start": v(-23, 9.5) * mm, "end": v(-23, 14.5) * mm, "construction": true});
            skSolve(sketch);
        }
        {
            var Q0;
            Q0 = qSketchRegion(id + "F38", true);
            extrude(context, id + "F39", {"entities" : qUnion([Q0]), "operationType" : NewBodyOperationType.REMOVE, "oppositeDirection" : true, "depth" : 3 * mm});
        }
        {
            var Q0;
            Q0=makeQuery(id+"F24.boolean.opBoolean","INTERSECT",EDGE,{"derivedFrom":[makeQuery(id+"F3.boolean.opBoolean","COPY",FACE,{"derivedFrom":makeQuery(id+"F3.opExtrude","CAP_FACE",FACE,{"disambiguationData":[OSD([sQuery(id+"F2.wireOp",EDGE,"E4"),sQuery(id+"F2.wireOp",EDGE,"E6.0"),sQuery(id+"F2.wireOp",EDGE,"E7"),sQuery(id+"F2.wireOp",EDGE,"E8")])],"isStart":false})}),makeQuery(id+"F24.opExtrude","SWEPT_FACE",FACE,{"disambiguationData":[OSD([sQuery(id+"F23.wireOp",EDGE,"E77.MirrorCS")])]})]});
            var Q1;
            Q1=makeQuery(id+"F24.boolean.opBoolean","INTERSECT",EDGE,{"derivedFrom":[makeQuery(id+"F3.boolean.opBoolean","COPY",FACE,{"derivedFrom":makeQuery(id+"F3.opExtrude","CAP_FACE",FACE,{"disambiguationData":[OSD([sQuery(id+"F2.wireOp",EDGE,"E4"),sQuery(id+"F2.wireOp",EDGE,"E6.0"),sQuery(id+"F2.wireOp",EDGE,"E7"),sQuery(id+"F2.wireOp",EDGE,"E8")])],"isStart":false})}),makeQuery(id+"F24.opExtrude","SWEPT_FACE",FACE,{"disambiguationData":[OSD([sQuery(id+"F23.wireOp",EDGE,"E76.MirrorCS")])]})]});
            var Q2;
            Q2=makeQuery(id+"F37.opExtrude","CAP_EDGE",EDGE,{"disambiguationData":[OSD([sQuery(id+"F36.wireOp",EDGE,"E110")])],"isStart":true});
            var Q3;
            Q3=makeQuery(id+"F24.boolean.opBoolean","INTERSECT",EDGE,{"derivedFrom":[makeQuery(id+"F3.boolean.opBoolean","COPY",FACE,{"derivedFrom":makeQuery(id+"F3.opExtrude","CAP_FACE",FACE,{"disambiguationData":[OSD([sQuery(id+"F2.wireOp",EDGE,"E4"),sQuery(id+"F2.wireOp",EDGE,"E6.0"),sQuery(id+"F2.wireOp",EDGE,"E7"),sQuery(id+"F2.wireOp",EDGE,"E8")])],"isStart":false})}),makeQuery(id+"F24.opExtrude","SWEPT_FACE",FACE,{"disambiguationData":[OSD([sQuery(id+"F23.wireOp",EDGE,"E73")])]})]});
            var Q4;
            Q4=makeQuery(id+"F24.boolean.opBoolean","INTERSECT",EDGE,{"derivedFrom":[makeQuery(id+"F3.boolean.opBoolean","COPY",FACE,{"derivedFrom":makeQuery(id+"F3.opExtrude","CAP_FACE",FACE,{"disambiguationData":[OSD([sQuery(id+"F2.wireOp",EDGE,"E4"),sQuery(id+"F2.wireOp",EDGE,"E6.0"),sQuery(id+"F2.wireOp",EDGE,"E7"),sQuery(id+"F2.wireOp",EDGE,"E8")])],"isStart":false})}),makeQuery(id+"F24.opExtrude","SWEPT_FACE",FACE,{"disambiguationData":[OSD([sQuery(id+"F23.wireOp",EDGE,"E72")])]})]});
            var Q5;
            Q5=makeQuery(id+"F37.opExtrude","CAP_EDGE",EDGE,{"disambiguationData":[OSD([sQuery(id+"F36.wireOp",EDGE,"E116")])],"isStart":true});
            fillet(context, id + "F40", {"entities" : qUnion([Q0, Q1, Q2, Q3, Q4, Q5]), "radius" : 2 * mm, "tangentPropagation" : true, "allowEdgeOverflow" : false});
        }
    });
